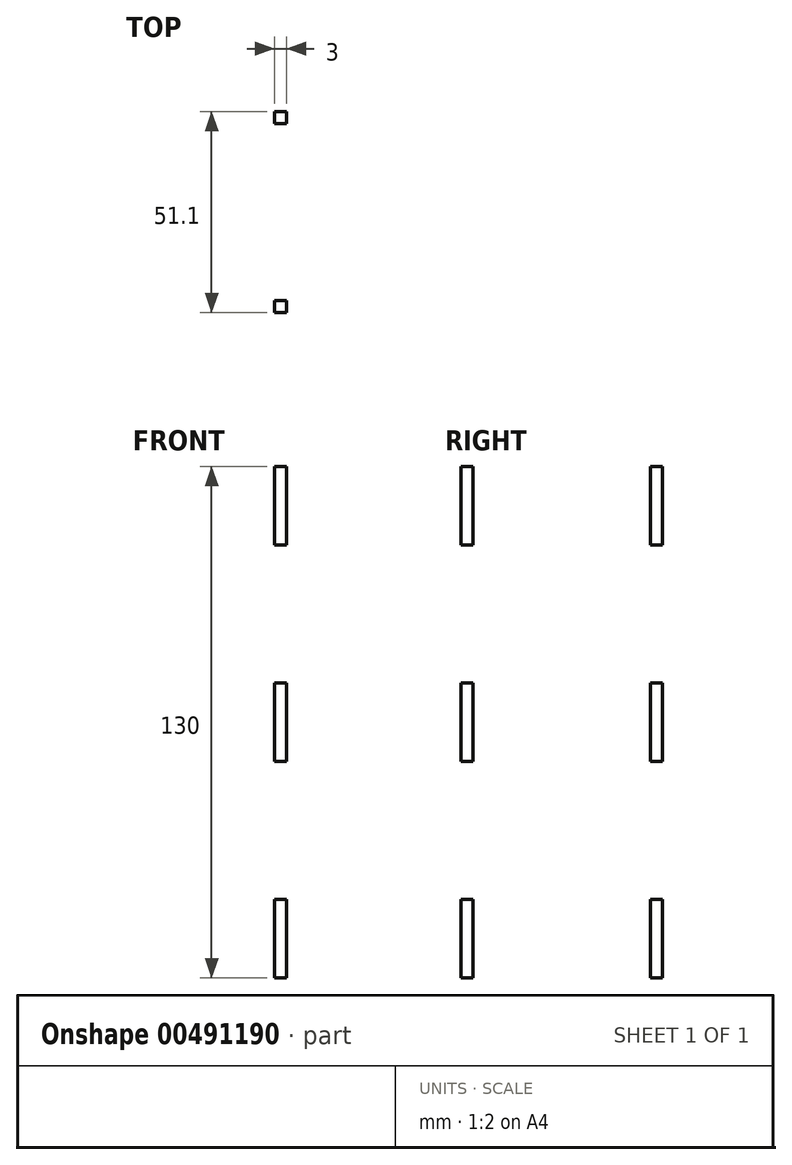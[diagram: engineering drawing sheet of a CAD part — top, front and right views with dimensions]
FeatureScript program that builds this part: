
annotation { "Feature Type Name" : "Feature", "Feature Type Description" : "" }
export const myFeature = defineFeature(function(context is Context, id is Id, definition is map)
    precondition{}
    {
        {
            var Q0;
            Q0=qCreatedBy(makeId("Right.planeOp"),FACE);
            var sketch = newSketch(context, id + "F0", { "sketchPlane" : qUnion([Q0])});
            skLineSegment(sketch, "E0.bottom", {"start": v(22.5, -100) * mm, "end": v(-22.5, -100) * mm});
            skLineSegment(sketch, "E0.top", {"start": v(22.5, 100) * mm, "end": v(-22.5, 100) * mm});
            skLineSegment(sketch, "E0.left", {"start": v(22.5, -100) * mm, "end": v(22.5, 100) * mm});
            skLineSegment(sketch, "E0.right", {"start": v(-22.5, -100) * mm, "end": v(-22.5, 100) * mm});
            skPoint(sketch, "E0.middle", {"position": v(0, 0) * mm});
            skLineSegment(sketch, "E1.bottom", {"start": v(-22.5, 45) * mm, "end": v(-25.55, 45) * mm});
            skLineSegment(sketch, "E1.top", {"start": v(-22.5, 65) * mm, "end": v(-25.55, 65) * mm});
            skLineSegment(sketch, "E1.left", {"start": v(-22.5, 45) * mm, "end": v(-22.5, 65) * mm});
            skLineSegment(sketch, "E1.right", {"start": v(-25.55, 45) * mm, "end": v(-25.55, 65) * mm});
            skPoint(sketch, "E1.middle", {"position": v(-24.02, 55) * mm});
            skLineSegment(sketch, "E2.bottom", {"start": v(-22.5, -10) * mm, "end": v(-25.55, -10) * mm});
            skLineSegment(sketch, "E2.top", {"start": v(-22.5, 10) * mm, "end": v(-25.55, 10) * mm});
            skLineSegment(sketch, "E2.left", {"start": v(-22.5, -10) * mm, "end": v(-22.5, 10) * mm});
            skLineSegment(sketch, "E2.right", {"start": v(-25.55, -10) * mm, "end": v(-25.55, 10) * mm});
            skPoint(sketch, "E2.middle", {"position": v(-24.02, 0) * mm});
            skLineSegment(sketch, "E3.bottom", {"start": v(-22.5, -65) * mm, "end": v(-25.55, -65) * mm});
            skLineSegment(sketch, "E3.top", {"start": v(-22.5, -45) * mm, "end": v(-25.55, -45) * mm});
            skLineSegment(sketch, "E3.left", {"start": v(-22.5, -65) * mm, "end": v(-22.5, -45) * mm});
            skLineSegment(sketch, "E3.right", {"start": v(-25.55, -65) * mm, "end": v(-25.55, -45) * mm});
            skPoint(sketch, "E3.middle", {"position": v(-24.02, -55) * mm});
            skLineSegment(sketch, "E4.bottom", {"start": v(25.55, 45) * mm, "end": v(22.5, 45) * mm});
            skLineSegment(sketch, "E4.top", {"start": v(25.55, 65) * mm, "end": v(22.5, 65) * mm});
            skLineSegment(sketch, "E4.left", {"start": v(25.55, 45) * mm, "end": v(25.55, 65) * mm});
            skLineSegment(sketch, "E4.right", {"start": v(22.5, 45) * mm, "end": v(22.5, 65) * mm});
            skPoint(sketch, "E4.middle", {"position": v(24.03, 55) * mm});
            skLineSegment(sketch, "E5.bottom", {"start": v(25.55, -10) * mm, "end": v(22.5, -10) * mm});
            skLineSegment(sketch, "E5.top", {"start": v(25.55, 10) * mm, "end": v(22.5, 10) * mm});
            skLineSegment(sketch, "E5.left", {"start": v(25.55, -10) * mm, "end": v(25.55, 10) * mm});
            skLineSegment(sketch, "E5.right", {"start": v(22.5, -10) * mm, "end": v(22.5, 10) * mm});
            skPoint(sketch, "E5.middle", {"position": v(24.03, 0) * mm});
            skLineSegment(sketch, "E6.bottom", {"start": v(25.55, -65) * mm, "end": v(22.5, -65) * mm});
            skLineSegment(sketch, "E6.top", {"start": v(25.55, -45) * mm, "end": v(22.5, -45) * mm});
            skLineSegment(sketch, "E6.left", {"start": v(25.55, -65) * mm, "end": v(25.55, -45) * mm});
            skLineSegment(sketch, "E6.right", {"start": v(22.5, -65) * mm, "end": v(22.5, -45) * mm});
            skPoint(sketch, "E6.middle", {"position": v(24.03, -55) * mm});
            skLineSegment(sketch, "E7.bottom", {"start": v(9.95, 100) * mm, "end": v(-9.95, 100) * mm});
            skLineSegment(sketch, "E7.top", {"start": v(9.95, 96.95) * mm, "end": v(-9.95, 96.95) * mm});
            skLineSegment(sketch, "E7.left", {"start": v(9.95, 100) * mm, "end": v(9.95, 96.95) * mm});
            skLineSegment(sketch, "E7.right", {"start": v(-9.95, 100) * mm, "end": v(-9.95, 96.95) * mm});
            skPoint(sketch, "E7.middle", {"position": v(0, 98.48) * mm});
            skLineSegment(sketch, "E8.bottom", {"start": v(9.95, -100) * mm, "end": v(-9.95, -100) * mm});
            skLineSegment(sketch, "E8.top", {"start": v(9.95, -96.95) * mm, "end": v(-9.95, -96.95) * mm});
            skLineSegment(sketch, "E8.left", {"start": v(9.95, -100) * mm, "end": v(9.95, -96.95) * mm});
            skLineSegment(sketch, "E8.right", {"start": v(-9.95, -100) * mm, "end": v(-9.95, -96.95) * mm});
            skPoint(sketch, "E8.middle", {"position": v(0, -98.48) * mm});
            skSolve(sketch);
        }
        {
            var Q0;
            Q0=makeQuery(id+"F0.imprint","IMPRINT",FACE,{"disambiguationData":[TD([[makeQuery(id+"F0.imprint","IMPRINT",EDGE,{"derivedFrom":sQuery(id+"F0.wireOp",EDGE,"E1.bottom")}),-1.0]])]});
            var Q1;
            Q1=makeQuery(id+"F0.imprint","IMPRINT",FACE,{"disambiguationData":[TD([[makeQuery(id+"F0.imprint","IMPRINT",EDGE,{"derivedFrom":sQuery(id+"F0.wireOp",EDGE,"E2.bottom")}),-1.0]])]});
            var Q2;
            Q2=makeQuery(id+"F0.imprint","IMPRINT",FACE,{"disambiguationData":[TD([[makeQuery(id+"F0.imprint","IMPRINT",EDGE,{"derivedFrom":sQuery(id+"F0.wireOp",EDGE,"E3.bottom")}),-1.0]])]});
            var Q3;
            Q3=makeQuery(id+"F0.imprint","IMPRINT",FACE,{"disambiguationData":[TD([[makeQuery(id+"F0.imprint","IMPRINT",EDGE,{"derivedFrom":sQuery(id+"F0.wireOp",EDGE,"E4.bottom")}),-1.0]])]});
            var Q4;
            Q4=makeQuery(id+"F0.imprint","IMPRINT",FACE,{"disambiguationData":[TD([[makeQuery(id+"F0.imprint","IMPRINT",EDGE,{"derivedFrom":sQuery(id+"F0.wireOp",EDGE,"E5.bottom")}),-1.0]])]});
            var Q5;
            Q5=makeQuery(id+"F0.imprint","IMPRINT",FACE,{"disambiguationData":[TD([[makeQuery(id+"F0.imprint","IMPRINT",EDGE,{"derivedFrom":sQuery(id+"F0.wireOp",EDGE,"E6.bottom")}),-1.0]])]});
            var Q6;
            {var subQ5=sQuery(id+"F0.wireOp",EDGE,"E1.left");Q6=makeQuery(id+"F0.imprint","IMPRINT",FACE,{"disambiguationData":[TD([[makeQuery(id+"F0.imprint","IMPRINT",EDGE,{"derivedFrom":subQ5}),-1.0]])]});}
            extrude(context, id + "F1", {"entities" : qUnion([Q0, Q1, Q2, Q3, Q4, Q5, Q6]), "depth" : 3 * mm});
        }
    });
